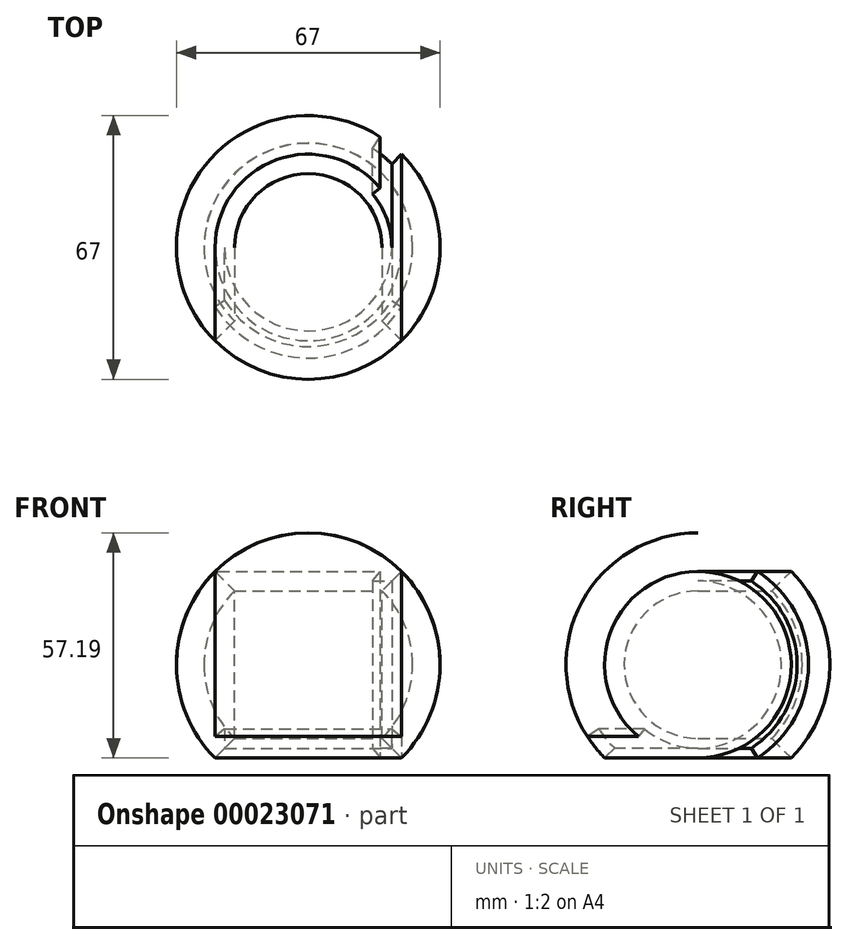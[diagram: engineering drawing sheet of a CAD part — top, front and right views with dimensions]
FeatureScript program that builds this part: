
annotation { "Feature Type Name" : "Feature", "Feature Type Description" : "" }
export const myFeature = defineFeature(function(context is Context, id is Id, definition is map)
    precondition{}
    {
        {
            var Q0;
            Q0=qCreatedBy(makeId("Front.planeOp"),FACE);
            var sketch = newSketch(context, id + "F0", { "sketchPlane" : qUnion([Q0])});
            skArc(sketch, "E0", {"start": v(-23.69, 23.69) * mm, "mid": v(-30.95, 12.82) * mm, "end": v(-33.5, 0) * mm});
            skLineSegment(sketch, "E1", {"start": v(-23.69, 23.69) * mm, "end": v(-18.74, 18.74) * mm});
            skLineSegment(sketch, "E2", {"start": v(23.69, 23.69) * mm, "end": v(18.74, 18.74) * mm});
            skArc(sketch, "E3.trimOffspring", {"start": v(33.5, 0) * mm, "mid": v(30.95, 12.82) * mm, "end": v(23.69, 23.69) * mm});
            skArc(sketch, "E4", {"start": v(26.5, 0) * mm, "mid": v(24.48, 10.14) * mm, "end": v(18.74, 18.74) * mm});
            skArc(sketch, "E5.trimOffspring", {"start": v(-18.74, 18.74) * mm, "mid": v(-24.48, 10.14) * mm, "end": v(-26.5, 0) * mm});
            skLineSegment(sketch, "E6", {"start": v(-33.5, 0) * mm, "end": v(-26.5, 0) * mm});
            skPoint(sketch, "E7.orphan", {"position": v(-58.83, 0) * mm});
            skLineSegment(sketch, "E8.trimOffspring", {"start": v(26.5, 0) * mm, "end": v(33.5, 0) * mm});
            skSolve(sketch);
        }
        {
            var Q0;
            Q0 = qSketchRegion(id + "F0", true);
            var Q1;
            Q1=sQuery(id+"F0.wireOp",EDGE,"E6");
            revolve(context, id + "F1", {"entities" : qUnion([Q0]), "axis" : qUnion([Q1]), "revolveType" : RevolveType.FULL});
        }
        {
            var Q0;
            Q0=qCreatedBy(makeId("Top.planeOp"),FACE);
            var sketch = newSketch(context, id + "F2", { "sketchPlane" : qUnion([Q0])});
            skArc(sketch, "E9", {"start": v(-23.69, 23.69) * mm, "mid": v(-33.5, 0) * mm, "end": v(-23.69, -23.69) * mm, "construction": true});
            skArc(sketch, "E10", {"start": v(23.69, -23.69) * mm, "mid": v(33.5, 0) * mm, "end": v(23.69, 23.69) * mm, "construction": true});
            skPoint(sketch, "E11", {"position": v(-33.5, 0) * mm});
            skPoint(sketch, "E12", {"position": v(33.5, 0) * mm});
            skArc(sketch, "E13", {"start": v(33.5, 0) * mm, "mid": v(0, 33.5) * mm, "end": v(-33.5, 0) * mm});
            skArc(sketch, "E14", {"start": v(-33.5, 0) * mm, "mid": v(0, -33.5) * mm, "end": v(33.5, 0) * mm});
            skSolve(sketch);
        }
        {
            var Q0;
            Q0=qCreatedBy(makeId("Front.planeOp"),FACE);
            var sketch = newSketch(context, id + "F3", { "sketchPlane" : qUnion([Q0])});
            skArc(sketch, "E15", {"start": v(-23.69, 23.69) * mm, "mid": v(-33.5, 0) * mm, "end": v(-23.69, -23.69) * mm});
            skLineSegment(sketch, "E16", {"start": v(-23.69, 23.69) * mm, "end": v(-18.74, 18.74) * mm});
            skLineSegment(sketch, "E17.0", {"start": v(-18.74, -18.74) * mm, "end": v(-18.74, 18.74) * mm});
            skLineSegment(sketch, "E18", {"start": v(-18.74, -18.74) * mm, "end": v(-23.69, -23.69) * mm});
            skArc(sketch, "E19", {"start": v(-18.74, 18.74) * mm, "mid": v(-26.5, 0) * mm, "end": v(-18.74, -18.74) * mm});
            skSolve(sketch);
        }
        {
            var Q0;
            Q0=makeQuery(id+"F3.imprint","IMPRINT",FACE,{"disambiguationData":[TD([[makeQuery(id+"F3.imprint","IMPRINT",EDGE,{"derivedFrom":sQuery(id+"F3.wireOp",EDGE,"E15")}),1.0]])]});
            var Q1;
            Q1=sQuery(id+"F2.wireOp",EDGE,"E13");
            sweep(context, id + "F4", {"operationType" : NewBodyOperationType.ADD, "profiles" : qUnion([Q0]), "path" : qUnion([Q1])});
        }
        {
            var Q0;
            Q0=qCreatedBy(makeId("Front.planeOp"),FACE);
            var sketch = newSketch(context, id + "F5", { "sketchPlane" : qUnion([Q0])});
            skLineSegment(sketch, "E20.0", {"start": v(-23.69, -23.69) * mm, "end": v(-21.21, -21.21) * mm});
            skPoint(sketch, "E21", {"position": v(-21.21, -21.21) * mm});
            skLineSegment(sketch, "E22", {"start": v(0, 0) * mm, "end": v(-41.3, -26.82) * mm, "construction": true});
            skPoint(sketch, "E23.orphan", {"position": v(-23.69, 23.69) * mm});
            skPoint(sketch, "E24.orphan", {"position": v(-18.74, 18.74) * mm});
            skPoint(sketch, "E25.0.start.orphan", {"position": v(-18.74, -18.74) * mm});
            skArc(sketch, "E26", {"start": v(-23.69, 23.69) * mm, "mid": v(0, -33.5) * mm, "end": v(23.69, 23.69) * mm});
            skLineSegment(sketch, "E27", {"start": v(-23.63, -15.35) * mm, "end": v(-28.1, -18.25) * mm});
            skArc(sketch, "E28", {"start": v(-25.16, -16.34) * mm, "mid": v(-23.31, -18.88) * mm, "end": v(-21.21, -21.21) * mm});
            skArc(sketch, "E29", {"start": v(-30.32, -19.7) * mm, "mid": v(-28.1, -22.75) * mm, "end": v(-25.57, -25.57) * mm});
            skLineSegment(sketch, "E30", {"start": v(-21.21, -21.21) * mm, "end": v(-25.57, -25.57) * mm});
            skLineSegment(sketch, "E31", {"start": v(-30.32, -19.7) * mm, "end": v(-28.1, -18.25) * mm});
            skLineSegment(sketch, "E32", {"start": v(58.3, 0) * mm, "end": v(-70.9, 0) * mm, "construction": true});
            skSolve(sketch);
        }
        {
            var Q0;
            {var subQ3=sQuery(id+"F5.wireOp",EDGE,"E28");Q0=makeQuery(id+"F5.imprint","IMPRINT",FACE,{"disambiguationData":[TD([[makeQuery(id+"F5.imprint","IMPRINT",EDGE,{"derivedFrom":subQ3}),-1.0]])]});}
            var Q1;
            Q1=sQuery(id+"F2.wireOp",EDGE,"E14");
            sweep(context, id + "F6", {"operationType" : NewBodyOperationType.ADD, "profiles" : qUnion([Q0]), "path" : qUnion([Q1])});
        }
        {
            var Q0;
            Q0=qCreatedBy(makeId("Top.planeOp"),FACE);
            var sketch = newSketch(context, id + "F7", { "sketchPlane" : qUnion([Q0])});
            skLineSegment(sketch, "E33", {"start": v(0, 0) * mm, "end": v(-35.73, 35.73) * mm, "construction": true});
            skLineSegment(sketch, "E34", {"start": v(0, 0) * mm, "end": v(-24.56, 37.82) * mm, "construction": true});
            skArc(sketch, "E35", {"start": v(18.74, -18.74) * mm, "mid": v(0, 26.5) * mm, "end": v(-18.74, -18.74) * mm});
            skArc(sketch, "E36", {"start": v(23.69, 23.69) * mm, "mid": v(21.08, 26.03) * mm, "end": v(18.25, 28.1) * mm});
            skLineSegment(sketch, "E37", {"start": v(-18.74, 18.74) * mm, "end": v(-23.69, 23.69) * mm});
            skPoint(sketch, "E38", {"position": v(-21.21, 21.21) * mm});
            skArc(sketch, "E39", {"start": v(-21.21, 21.21) * mm, "mid": v(-23.31, -18.88) * mm, "end": v(16.34, -25.16) * mm});
            skLineSegment(sketch, "E40", {"start": v(-16.34, 25.16) * mm, "end": v(-18.25, 28.1) * mm});
            skLineSegment(sketch, "E41", {"start": v(0, 0) * mm, "end": v(-57.31, 0) * mm, "construction": true});
            skPoint(sketch, "E42", {"position": v(23.69, 23.69) * mm});
            skPoint(sketch, "E43", {"position": v(18.25, 28.1) * mm});
            skPoint(sketch, "E44", {"position": v(21.21, 21.21) * mm});
            skLineSegment(sketch, "E45", {"start": v(23.69, 23.69) * mm, "end": v(21.21, 21.21) * mm});
            skLineSegment(sketch, "E46", {"start": v(18.25, 28.1) * mm, "end": v(16.34, 25.16) * mm});
            skArc(sketch, "E47", {"start": v(-16.34, 25.16) * mm, "mid": v(-25.16, -16.34) * mm, "end": v(16.34, -25.16) * mm});
            skArc(sketch, "E48.trimOffspring", {"start": v(-18.25, 28.1) * mm, "mid": v(-33.32, 3.5) * mm, "end": v(-23.69, -23.69) * mm});
            skArc(sketch, "E49", {"start": v(21.21, 21.21) * mm, "mid": v(18.88, 23.31) * mm, "end": v(16.34, 25.16) * mm});
            skSolve(sketch);
        }
        {
            var Q0;
            Q0=makeQuery(id+"F7.imprint","IMPRINT",FACE,{"disambiguationData":[TD([[makeQuery(id+"F7.imprint","IMPRINT",EDGE,{"derivedFrom":sQuery(id+"F7.wireOp",EDGE,"E36")}),1.0]])]});
            var Q1;
            Q1=sQuery(id+"F5.wireOp",EDGE,"E32");
            revolve(context, id + "F8", {"operationType" : NewBodyOperationType.REMOVE, "entities" : qUnion([Q0]), "axis" : qUnion([Q1]), "revolveType" : RevolveType.SYMMETRIC, "oppositeDirection" : true, "angle" : 180 * degree});
        }
    });
